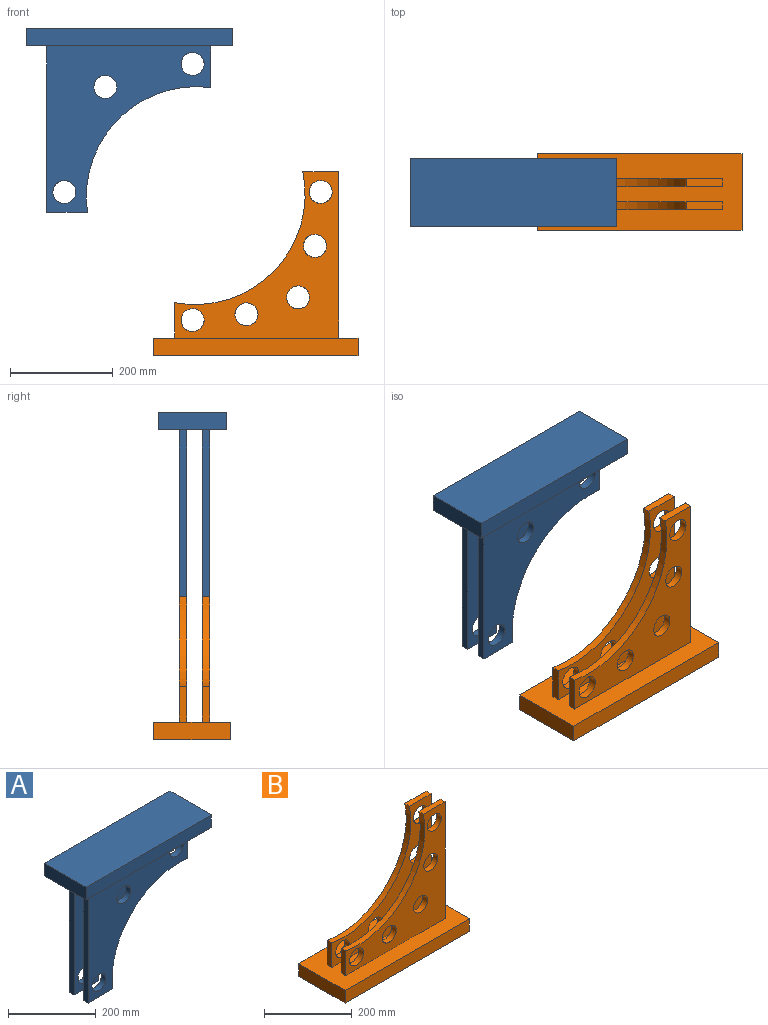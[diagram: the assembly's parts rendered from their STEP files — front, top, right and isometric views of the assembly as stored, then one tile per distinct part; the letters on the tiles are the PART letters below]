
ASSEMBLY  parts=2 mates=3
PART A: 24 faces, bbox 403.9x133.2x360 mm
  f0: plane 81.14x15mm, normal (1,0,0), area 1217.1mm2, adj f6,f7,f20,f23
  f1: plane 325x15mm, normal (-1,0,0), area 4875mm2, adj f10,f11,f20,f22
  f2: plane 80x15mm, normal (0,0,-1), area 1200mm2, adj f6,f7,f9,f23
  f3: cylinder r=22.5mm len=45mm, axis (0,-1,0), area 2120.6mm2, adj f7,f23
  f4: cylinder r=22.5mm len=45mm, axis (0,-1,0), area 2120.6mm2, adj f7,f23
  f5: cylinder r=22.5mm len=45mm, axis (0,-1,0), area 2120.6mm2, adj f7,f23
  f6: cylinder r=215mm len=245.59mm, axis (0,-1,0), area 5935mm2, adj f0,f2,f7,f23
  f7: plane 325x320mm, normal (0,1,0), area 49709.2mm2, adj f0,f2,f3,f4,f5,f6,f9,f20
  f8: plane 81.14x15mm, normal (1,0,0), area 1217.1mm2, adj f10,f15,f20,f22
  f9: plane 325x15mm, normal (-1,0,0), area 4875mm2, adj f2,f7,f20,f23
  f10: plane 325x320mm, normal (0,-1,0), area 49709.2mm2, adj f1,f8,f11,f12,f13,f14,f15,f20
  f11: plane 80x15mm, normal (0,0,-1), area 1200mm2, adj f1,f10,f15,f22
  f12: cylinder r=22.5mm len=45mm, axis (0,-1,0), area 2120.6mm2, adj f10,f22
  f13: cylinder r=22.5mm len=45mm, axis (0,-1,0), area 2120.6mm2, adj f10,f22
  f14: cylinder r=22.5mm len=45mm, axis (0,-1,0), area 2120.6mm2, adj f10,f22
  f15: cylinder r=215mm len=245.59mm, axis (0,-1,0), area 5935mm2, adj f8,f10,f11,f22
  f16: plane 133.21x35mm, normal (-1,0,0), area 4662.4mm2, adj f17,f19,f20,f21
  f17: plane 403.91x35mm, normal (0,-1,0), area 14136.9mm2, adj f16,f18,f20,f21
  f18: plane 133.21x35mm, normal (1,0,0), area 4662.4mm2, adj f17,f19,f20,f21
  f19: plane 403.91x35mm, normal (0,1,0), area 14136.9mm2, adj f16,f18,f20,f21
  f20: plane 403.91x133.21mm, normal (0,0,-1), area 44205.5mm2, adj f0,f1,f7,f8,f9,f10,f16,f17
  f21: plane 403.91x133.21mm, normal (0,0,1), area 53805.5mm2, adj f16,f17,f18,f19
  f22: plane 325x320mm, normal (0,1,0), area 49709.2mm2, adj f1,f8,f11,f12,f13,f14,f15,f20
  f23: plane 325x320mm, normal (0,-1,0), area 49709.2mm2, adj f0,f2,f3,f4,f5,f6,f9,f20
PART B: 28 faces, bbox 399.7x149.2x360 mm
  f0: plane 325x320mm, normal (0,-1,0), area 39957mm2, adj f1,f2,f4,f5,f6,f7,f8,f9
  f1: plane 325x15mm, normal (1,0,0), area 4875mm2, adj f0,f3,f10,f26
  f2: plane 69.05x15mm, normal (-1,0,0), area 1035.7mm2, adj f0,f3,f9,f26
  f3: plane 325x320mm, normal (0,1,0), area 39957mm2, adj f1,f2,f4,f5,f6,f7,f8,f9
  f4: cylinder r=22.5mm len=45mm, axis (0,-1,0), area 2120.6mm2, adj f0,f3
  f5: cylinder r=22.5mm len=45mm, axis (0,-1,0), area 2120.6mm2, adj f0,f3
  f6: cylinder r=22.5mm len=45mm, axis (0,-1,0), area 2120.6mm2, adj f0,f3
  f7: cylinder r=22.5mm len=45mm, axis (0,-1,0), area 2120.6mm2, adj f0,f3
  f8: cylinder r=22.5mm len=45mm, axis (0,-1,0), area 2120.6mm2, adj f0,f3
  f9: cylinder r=215mm len=259.65mm, axis (0,1,0), area 6339.2mm2, adj f0,f2,f3,f10
  f10: plane 70x15mm, normal (0,0,1), area 1050mm2, adj f0,f1,f3,f9
  f11: plane 69.05x15mm, normal (-1,0,0), area 1035.7mm2, adj f13,f14,f21,f26
  f12: plane 325x15mm, normal (1,0,0), area 4875mm2, adj f13,f14,f15,f26
  f13: plane 325x320mm, normal (0,1,0), area 39957mm2, adj f11,f12,f15,f16,f17,f18,f19,f20
  f14: plane 325x320mm, normal (0,-1,0), area 39957mm2, adj f11,f12,f15,f16,f17,f18,f19,f20
  f15: plane 70x15mm, normal (0,0,1), area 1050mm2, adj f12,f13,f14,f21
  f16: cylinder r=22.5mm len=45mm, axis (0,-1,0), area 2120.6mm2, adj f13,f14
  f17: cylinder r=22.5mm len=45mm, axis (0,-1,0), area 2120.6mm2, adj f13,f14
  f18: cylinder r=22.5mm len=45mm, axis (0,-1,0), area 2120.6mm2, adj f13,f14
  f19: cylinder r=22.5mm len=45mm, axis (0,-1,0), area 2120.6mm2, adj f13,f14
  f20: cylinder r=22.5mm len=45mm, axis (0,-1,0), area 2120.6mm2, adj f13,f14
  f21: cylinder r=215mm len=259.65mm, axis (0,1,0), area 6339.2mm2, adj f11,f13,f14,f15
  f22: plane 149.23x35mm, normal (-1,0,0), area 5223mm2, adj f23,f25,f26,f27
  f23: plane 399.74x35mm, normal (0,1,0), area 13990.8mm2, adj f22,f24,f26,f27
  f24: plane 149.23x35mm, normal (1,0,0), area 5223mm2, adj f23,f25,f26,f27
  f25: plane 399.74x35mm, normal (0,-1,0), area 13990.8mm2, adj f22,f24,f26,f27
  f26: plane 399.74x149.23mm, normal (0,0,1), area 50052.1mm2, adj f0,f1,f2,f3,f11,f12,f13,f14
  f27: plane 399.74x149.23mm, normal (0,0,-1), area 59652.1mm2, adj f22,f23,f24,f25
PLACE A t=(-72.99,552.38,208.11)mm
PLACE B t=(177.01,618.18,-71.89)mm fixed
MATE planar B.f7 <-> A.f4  axis (0,-1,0) through (-107.99,524.61,-1.89)mm
MATE planar B.f0 <-> A.f10  axis (0,-1,0) through (75.66,517.11,66.94)mm
MATE planar B.f8 <-> A.f5  axis (0,-1,0) through (142.01,524.61,248.11)mm
